# Revit family: NXPOE7-24B
name_source: partatom
category: Communication Devices
revit_build: Autodesk Revit 2014 (Build: 20130308_1515(x64)
units: mm (PartAtom-declared; Revit-internal decimal feet)

## types (1)
- NXPOE7-24B
    Assembly Code = D5090
    Connectivity = Cat5 Pins 4, 5, 6, 7 and 8
    Default Elevation = 48 "
    Description = NX network accessory that provides for splitting the HubbNET™ network
from the NXAC into multiple segments
    Features = NX network accessory that provides for splitting the HubbNET™ network
from the NXAC into multiple segments
• 24V power is provided to the unit via a five amp computer style plug-in
power supply
• Provides seven powered RJ45 ports for connection of NX network devices
• Multiple dimming options including DMX to less than 0.1%
• Limit of 64 NXHNB2 Network Bridge modules per segment ENERGY STAR®
certified configurations
• Expands the capacity of the NXAC to 448 bridges suitable for large
commercial and architectural interiors
    Housing Material = Paint - Hubbell - Carbon Black
    Manufacturer = Hubbell Control Solutions
    Model = NXPOE
    Product Documentation Link = https://hubbellcdn.com
    Product Page URL = https://www.hubbell.com
    Type Comments = NX POE SWITCH/POWER INJECTOR
    URL = https://www.hubbell.com
    Voltage = 24V
    Warranty = 5-Years Warranty
    Washer = Metal-Hubbell-Galvanized_Steel

## geometry (parser evidence)
native form markers: Sweep x1
no freeform markers — native parametric forms only
